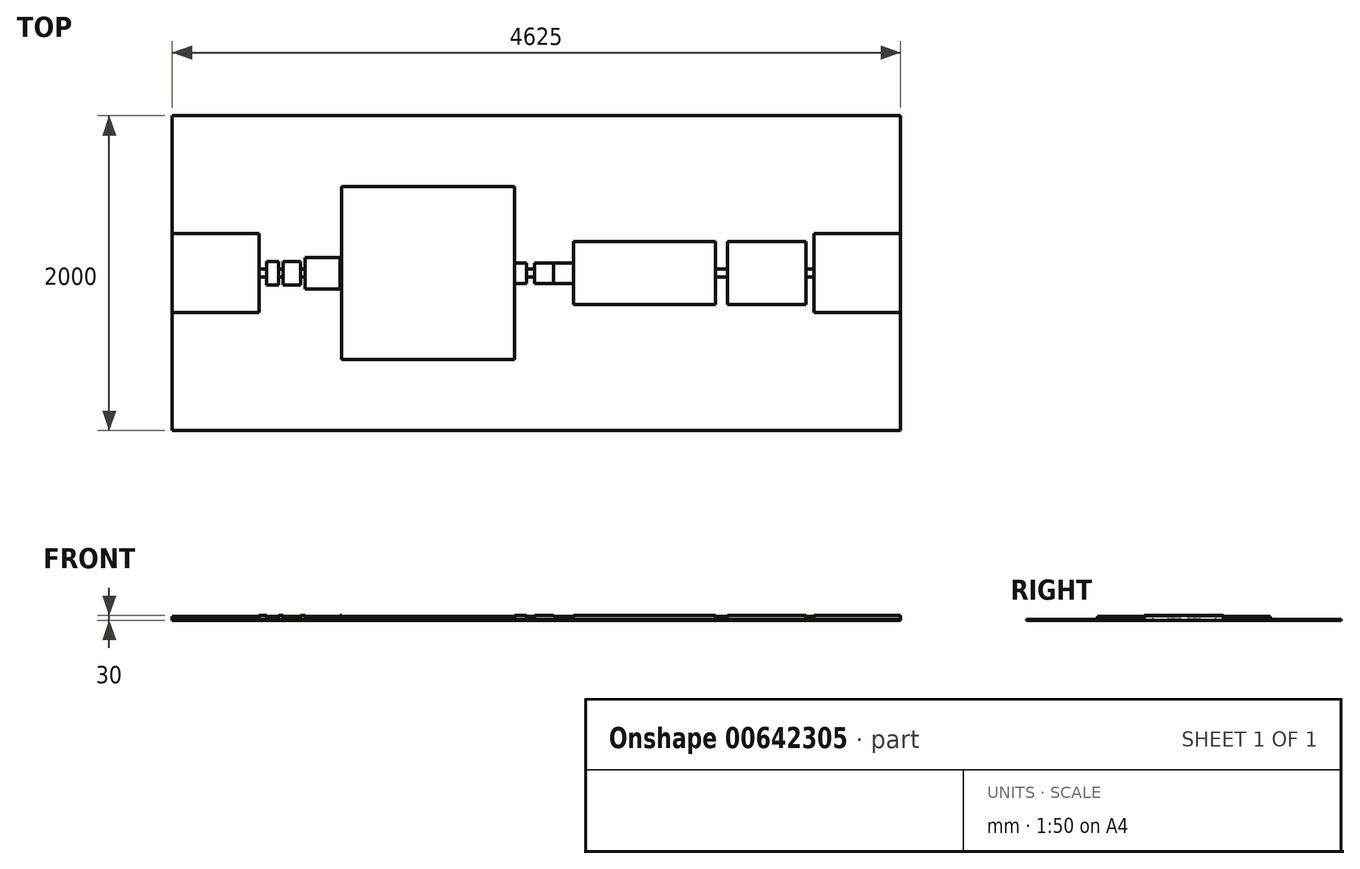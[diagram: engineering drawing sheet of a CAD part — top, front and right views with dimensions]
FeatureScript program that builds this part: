
annotation { "Feature Type Name" : "Feature", "Feature Type Description" : "" }
export const myFeature = defineFeature(function(context is Context, id is Id, definition is map)
    precondition{}
    {
        {
            var Q0;
            Q0=qCreatedBy(makeId("Top.planeOp"),FACE);
            var sketch = newSketch(context, id + "F0", { "sketchPlane" : qUnion([Q0])});
            skLineSegment(sketch, "E0.bottom", {"start": v(0, 1000) * mm, "end": v(4625, 1000) * mm});
            skLineSegment(sketch, "E0.top", {"start": v(0, -1000) * mm, "end": v(4625, -1000) * mm});
            skLineSegment(sketch, "E0.left", {"start": v(0, 1000) * mm, "end": v(0, -1000) * mm});
            skLineSegment(sketch, "E0.right", {"start": v(4625, 1000) * mm, "end": v(4625, -1000) * mm});
            skLineSegment(sketch, "E1", {"start": v(0, 0) * mm, "end": v(4625, 0) * mm, "construction": true});
            skLineSegment(sketch, "E2.bottom", {"start": v(550, -250) * mm, "end": v(0, -250) * mm});
            skLineSegment(sketch, "E2.top", {"start": v(550, 250) * mm, "end": v(0, 250) * mm});
            skLineSegment(sketch, "E2.left", {"start": v(550, -250) * mm, "end": v(550, 250) * mm});
            skLineSegment(sketch, "E2.right", {"start": v(0, -250) * mm, "end": v(0, 250) * mm});
            skPoint(sketch, "E2.middle", {"position": v(275, 0) * mm});
            skLineSegment(sketch, "E3.bottom", {"start": v(2175, -550) * mm, "end": v(1075, -550) * mm});
            skLineSegment(sketch, "E3.top", {"start": v(2175, 550) * mm, "end": v(1075, 550) * mm});
            skLineSegment(sketch, "E3.left", {"start": v(2175, -550) * mm, "end": v(2175, 550) * mm});
            skLineSegment(sketch, "E3.right", {"start": v(1075, -550) * mm, "end": v(1075, 550) * mm});
            skPoint(sketch, "E3.middle", {"position": v(1625, 0) * mm});
            skLineSegment(sketch, "E4.bottom", {"start": v(4625, -250) * mm, "end": v(4075, -250) * mm});
            skLineSegment(sketch, "E4.top", {"start": v(4625, 250) * mm, "end": v(4075, 250) * mm});
            skLineSegment(sketch, "E4.left", {"start": v(4625, -250) * mm, "end": v(4625, 250) * mm});
            skLineSegment(sketch, "E4.right", {"start": v(4075, -250) * mm, "end": v(4075, 250) * mm});
            skPoint(sketch, "E4.middle", {"position": v(4350, 0) * mm});
            skLineSegment(sketch, "E5.bottom", {"start": v(675, -75) * mm, "end": v(600, -75) * mm});
            skLineSegment(sketch, "E5.top", {"start": v(675, 75) * mm, "end": v(600, 75) * mm});
            skLineSegment(sketch, "E5.left", {"start": v(675, -75) * mm, "end": v(675, 75) * mm});
            skLineSegment(sketch, "E5.right", {"start": v(600, -75) * mm, "end": v(600, 75) * mm});
            skPoint(sketch, "E5.middle", {"position": v(637.5, 0) * mm});
            skLineSegment(sketch, "E6.bottom", {"start": v(600, -25) * mm, "end": v(550, -25) * mm});
            skLineSegment(sketch, "E6.top", {"start": v(600, 25) * mm, "end": v(550, 25) * mm});
            skLineSegment(sketch, "E6.left", {"start": v(600, -25) * mm, "end": v(600, 25) * mm});
            skLineSegment(sketch, "E6.right", {"start": v(550, -25) * mm, "end": v(550, 25) * mm});
            skPoint(sketch, "E6.middle", {"position": v(575, 0) * mm});
            skLineSegment(sketch, "E7.bottom", {"start": v(675, 25) * mm, "end": v(705, 25) * mm});
            skLineSegment(sketch, "E7.top", {"start": v(675, -25) * mm, "end": v(705, -25) * mm});
            skLineSegment(sketch, "E7.left", {"start": v(675, 25) * mm, "end": v(675, -25) * mm});
            skLineSegment(sketch, "E7.right", {"start": v(705, 25) * mm, "end": v(705, -25) * mm});
            skPoint(sketch, "E7.middle", {"position": v(690, 0) * mm});
            skLineSegment(sketch, "E8.bottom", {"start": v(705, 75) * mm, "end": v(815, 75) * mm});
            skLineSegment(sketch, "E8.top", {"start": v(705, -75) * mm, "end": v(815, -75) * mm});
            skLineSegment(sketch, "E8.left", {"start": v(705, 75) * mm, "end": v(705, -75) * mm});
            skLineSegment(sketch, "E8.right", {"start": v(815, 75) * mm, "end": v(815, -75) * mm});
            skPoint(sketch, "E8.middle", {"position": v(760, 0) * mm});
            skLineSegment(sketch, "E9.bottom", {"start": v(815, 25) * mm, "end": v(845, 25) * mm});
            skLineSegment(sketch, "E9.top", {"start": v(815, -25) * mm, "end": v(845, -25) * mm});
            skLineSegment(sketch, "E9.left", {"start": v(815, 25) * mm, "end": v(815, -25) * mm});
            skLineSegment(sketch, "E9.right", {"start": v(845, 25) * mm, "end": v(845, -25) * mm});
            skPoint(sketch, "E9.middle", {"position": v(830, 0) * mm});
            skLineSegment(sketch, "E10.bottom", {"start": v(845, 100) * mm, "end": v(1065, 100) * mm});
            skLineSegment(sketch, "E10.top", {"start": v(845, -100) * mm, "end": v(1065, -100) * mm});
            skLineSegment(sketch, "E10.left", {"start": v(845, 100) * mm, "end": v(845, -100) * mm});
            skLineSegment(sketch, "E10.right", {"start": v(1065, 100) * mm, "end": v(1065, -100) * mm});
            skPoint(sketch, "E10.middle", {"position": v(955, 0) * mm});
            skLineSegment(sketch, "E11.bottom", {"start": v(1065, 25) * mm, "end": v(1075, 25) * mm});
            skLineSegment(sketch, "E11.top", {"start": v(1065, -25) * mm, "end": v(1075, -25) * mm});
            skLineSegment(sketch, "E11.left", {"start": v(1065, 25) * mm, "end": v(1065, -25) * mm});
            skLineSegment(sketch, "E11.right", {"start": v(1075, 25) * mm, "end": v(1075, -25) * mm});
            skPoint(sketch, "E11.middle", {"position": v(1070, 0) * mm});
            skLineSegment(sketch, "E12.bottom", {"start": v(3450, -200) * mm, "end": v(2550, -200) * mm});
            skLineSegment(sketch, "E12.top", {"start": v(3450, 200) * mm, "end": v(2550, 200) * mm});
            skLineSegment(sketch, "E12.left", {"start": v(3450, -200) * mm, "end": v(3450, 200) * mm});
            skLineSegment(sketch, "E12.right", {"start": v(2550, -200) * mm, "end": v(2550, 200) * mm});
            skPoint(sketch, "E12.middle", {"position": v(3000, 0) * mm});
            skLineSegment(sketch, "E13.bottom", {"start": v(2075, -450) * mm, "end": v(1175, -450) * mm, "construction": true});
            skLineSegment(sketch, "E13.top", {"start": v(2075, 450) * mm, "end": v(1175, 450) * mm, "construction": true});
            skLineSegment(sketch, "E13.left", {"start": v(2075, -450) * mm, "end": v(2075, 450) * mm, "construction": true});
            skLineSegment(sketch, "E13.right", {"start": v(1175, -450) * mm, "end": v(1175, 450) * mm, "construction": true});
            skLineSegment(sketch, "E14.bottom", {"start": v(4025, -200) * mm, "end": v(3525, -200) * mm});
            skLineSegment(sketch, "E14.top", {"start": v(4025, 200) * mm, "end": v(3525, 200) * mm});
            skLineSegment(sketch, "E14.left", {"start": v(4025, -200) * mm, "end": v(4025, 200) * mm});
            skLineSegment(sketch, "E14.right", {"start": v(3525, -200) * mm, "end": v(3525, 200) * mm});
            skPoint(sketch, "E14.middle", {"position": v(3775, 0) * mm});
            skLineSegment(sketch, "E15.bottom", {"start": v(4025, 25) * mm, "end": v(4075, 25) * mm});
            skLineSegment(sketch, "E15.top", {"start": v(4025, -25) * mm, "end": v(4075, -25) * mm});
            skLineSegment(sketch, "E15.left", {"start": v(4025, 25) * mm, "end": v(4025, -25) * mm});
            skLineSegment(sketch, "E15.right", {"start": v(4075, 25) * mm, "end": v(4075, -25) * mm});
            skPoint(sketch, "E15.middle", {"position": v(4050, 0) * mm});
            skLineSegment(sketch, "E16.bottom", {"start": v(3450, 25) * mm, "end": v(3525, 25) * mm});
            skLineSegment(sketch, "E16.top", {"start": v(3450, -25) * mm, "end": v(3525, -25) * mm});
            skLineSegment(sketch, "E16.left", {"start": v(3450, 25) * mm, "end": v(3450, -25) * mm});
            skLineSegment(sketch, "E16.right", {"start": v(3525, 25) * mm, "end": v(3525, -25) * mm});
            skLineSegment(sketch, "E17.bottom", {"start": v(2550, -65) * mm, "end": v(2420, -65) * mm});
            skLineSegment(sketch, "E17.top", {"start": v(2550, 65) * mm, "end": v(2420, 65) * mm});
            skLineSegment(sketch, "E17.left", {"start": v(2550, -65) * mm, "end": v(2550, 65) * mm});
            skLineSegment(sketch, "E17.right", {"start": v(2420, -65) * mm, "end": v(2420, 65) * mm});
            skPoint(sketch, "E17.middle", {"position": v(2485, 0) * mm});
            skLineSegment(sketch, "E18.bottom", {"start": v(2250, -65) * mm, "end": v(2175, -65) * mm});
            skLineSegment(sketch, "E18.top", {"start": v(2250, 65) * mm, "end": v(2175, 65) * mm});
            skLineSegment(sketch, "E18.left", {"start": v(2250, -65) * mm, "end": v(2250, 65) * mm});
            skLineSegment(sketch, "E18.right", {"start": v(2175, -65) * mm, "end": v(2175, 65) * mm});
            skPoint(sketch, "E18.middle", {"position": v(2212.5, 0) * mm});
            skLineSegment(sketch, "E19.bottom", {"start": v(2420, -65) * mm, "end": v(2300, -65) * mm});
            skLineSegment(sketch, "E19.top", {"start": v(2420, 65) * mm, "end": v(2300, 65) * mm});
            skLineSegment(sketch, "E19.right", {"start": v(2300, -65) * mm, "end": v(2300, 65) * mm});
            skPoint(sketch, "E19.middle", {"position": v(2360, 0) * mm});
            skLineSegment(sketch, "E20.bottom", {"start": v(2250, 25) * mm, "end": v(2300, 25) * mm});
            skLineSegment(sketch, "E20.top", {"start": v(2250, -25) * mm, "end": v(2300, -25) * mm});
            skLineSegment(sketch, "E20.left", {"start": v(2250, 25) * mm, "end": v(2250, -25) * mm});
            skLineSegment(sketch, "E20.right", {"start": v(2300, 25) * mm, "end": v(2300, -25) * mm});
            skPoint(sketch, "E20.middle", {"position": v(2275, 0) * mm});
            skSolve(sketch);
        }
        {
            var Q0;
            {var subQ3=sQuery(id+"F0.wireOp",EDGE,"E2.bottom");Q0=makeQuery(id+"F0.imprint","IMPRINT",FACE,{"disambiguationData":[TD([[makeQuery(id+"F0.imprint","IMPRINT",EDGE,{"derivedFrom":subQ3}),-1.0]])]});}
            var Q1;
            Q1=makeQuery(id+"F0.imprint","IMPRINT",FACE,{"disambiguationData":[TD([[makeQuery(id+"F0.imprint","IMPRINT",EDGE,{"derivedFrom":sQuery(id+"F0.wireOp",EDGE,"E6.bottom")}),-1.0]])]});
            var Q2;
            {var subQ3=sQuery(id+"F0.wireOp",EDGE,"E5.bottom");Q2=makeQuery(id+"F0.imprint","IMPRINT",FACE,{"disambiguationData":[TD([[makeQuery(id+"F0.imprint","IMPRINT",EDGE,{"derivedFrom":subQ3}),-1.0]])]});}
            var Q3;
            {var subQ0=sQuery(id+"F0.wireOp",EDGE,"E7.bottom");Q3=makeQuery(id+"F0.imprint","IMPRINT",FACE,{"disambiguationData":[TD([[makeQuery(id+"F0.imprint","IMPRINT",EDGE,{"derivedFrom":subQ0}),-1.0]])]});}
            var Q4;
            {var subQ3=sQuery(id+"F0.wireOp",EDGE,"E8.bottom");Q4=makeQuery(id+"F0.imprint","IMPRINT",FACE,{"disambiguationData":[TD([[makeQuery(id+"F0.imprint","IMPRINT",EDGE,{"derivedFrom":subQ3}),-1.0]])]});}
            var Q5;
            {var subQ0=sQuery(id+"F0.wireOp",EDGE,"E9.bottom");Q5=makeQuery(id+"F0.imprint","IMPRINT",FACE,{"disambiguationData":[TD([[makeQuery(id+"F0.imprint","IMPRINT",EDGE,{"derivedFrom":subQ0}),-1.0]])]});}
            var Q6;
            {var subQ3=sQuery(id+"F0.wireOp",EDGE,"E10.bottom");Q6=makeQuery(id+"F0.imprint","IMPRINT",FACE,{"disambiguationData":[TD([[makeQuery(id+"F0.imprint","IMPRINT",EDGE,{"derivedFrom":subQ3}),-1.0]])]});}
            var Q7;
            Q7=makeQuery(id+"F0.imprint","IMPRINT",FACE,{"disambiguationData":[TD([[makeQuery(id+"F0.imprint","IMPRINT",EDGE,{"derivedFrom":sQuery(id+"F0.wireOp",EDGE,"E11.bottom")}),-1.0]])]});
            var Q8;
            {var subQ3=sQuery(id+"F0.wireOp",EDGE,"E3.bottom");Q8=makeQuery(id+"F0.imprint","IMPRINT",FACE,{"disambiguationData":[TD([[makeQuery(id+"F0.imprint","IMPRINT",EDGE,{"derivedFrom":subQ3}),-1.0]])]});}
            var Q9;
            {var subQ3=sQuery(id+"F0.wireOp",EDGE,"E18.bottom");Q9=makeQuery(id+"F0.imprint","IMPRINT",FACE,{"disambiguationData":[TD([[makeQuery(id+"F0.imprint","IMPRINT",EDGE,{"derivedFrom":subQ3}),-1.0]])]});}
            var Q10;
            Q10=makeQuery(id+"F0.imprint","IMPRINT",FACE,{"disambiguationData":[TD([[makeQuery(id+"F0.imprint","IMPRINT",EDGE,{"derivedFrom":sQuery(id+"F0.wireOp",EDGE,"E20.bottom")}),-1.0]])]});
            var Q11;
            {var subQ1=sQuery(id+"F0.wireOp",EDGE,"E19.bottom");Q11=makeQuery(id+"F0.imprint","IMPRINT",FACE,{"disambiguationData":[TD([[makeQuery(id+"F0.imprint","IMPRINT",EDGE,{"derivedFrom":subQ1}),-1.0]])]});}
            var Q12;
            Q12=makeQuery(id+"F0.imprint","IMPRINT",FACE,{"disambiguationData":[TD([[makeQuery(id+"F0.imprint","IMPRINT",EDGE,{"derivedFrom":sQuery(id+"F0.wireOp",EDGE,"E17.bottom")}),-1.0]])]});
            var Q13;
            {var subQ3=sQuery(id+"F0.wireOp",EDGE,"E12.bottom");Q13=makeQuery(id+"F0.imprint","IMPRINT",FACE,{"disambiguationData":[TD([[makeQuery(id+"F0.imprint","IMPRINT",EDGE,{"derivedFrom":subQ3}),-1.0]])]});}
            var Q14;
            Q14=makeQuery(id+"F0.imprint","IMPRINT",FACE,{"disambiguationData":[TD([[makeQuery(id+"F0.imprint","IMPRINT",EDGE,{"derivedFrom":sQuery(id+"F0.wireOp",EDGE,"E16.bottom")}),-1.0]])]});
            var Q15;
            {var subQ3=sQuery(id+"F0.wireOp",EDGE,"E14.bottom");Q15=makeQuery(id+"F0.imprint","IMPRINT",FACE,{"disambiguationData":[TD([[makeQuery(id+"F0.imprint","IMPRINT",EDGE,{"derivedFrom":subQ3}),-1.0]])]});}
            var Q16;
            Q16=makeQuery(id+"F0.imprint","IMPRINT",FACE,{"disambiguationData":[TD([[makeQuery(id+"F0.imprint","IMPRINT",EDGE,{"derivedFrom":sQuery(id+"F0.wireOp",EDGE,"E15.bottom")}),-1.0]])]});
            var Q17;
            {var subQ1=sQuery(id+"F0.wireOp",EDGE,"E4.bottom");Q17=makeQuery(id+"F0.imprint","IMPRINT",FACE,{"disambiguationData":[TD([[makeQuery(id+"F0.imprint","IMPRINT",EDGE,{"derivedFrom":subQ1}),-1.0]])]});}
            extrude(context, id + "F1", {"entities" : qUnion([Q0, Q1, Q2, Q3, Q4, Q5, Q6, Q7, Q8, Q9, Q10, Q11, Q12, Q13, Q14, Q15, Q16, Q17]), "depth" : 25 * mm, "offsetDistance" : 25 * mm});
        }
        {
            var Q0;
            Q0 = qSketchRegion(id + "F0", true);
            extrude(context, id + "F2", {"entities" : qUnion([Q0]), "operationType" : NewBodyOperationType.ADD, "depth" : 5 * mm, "offsetDistance" : 25 * mm});
        }
        {
            var Q0;
            Q0=makeQuery(id+"F0.imprint","IMPRINT",FACE,{"disambiguationData":[TD([[makeQuery(id+"F0.imprint","IMPRINT",EDGE,{"derivedFrom":sQuery(id+"F0.wireOp",EDGE,"E6.bottom")}),-1.0]])]});
            var Q1;
            {var subQ0=sQuery(id+"F0.wireOp",EDGE,"E7.bottom");Q1=makeQuery(id+"F0.imprint","IMPRINT",FACE,{"disambiguationData":[TD([[makeQuery(id+"F0.imprint","IMPRINT",EDGE,{"derivedFrom":subQ0}),-1.0]])]});}
            var Q2;
            {var subQ0=sQuery(id+"F0.wireOp",EDGE,"E9.bottom");Q2=makeQuery(id+"F0.imprint","IMPRINT",FACE,{"disambiguationData":[TD([[makeQuery(id+"F0.imprint","IMPRINT",EDGE,{"derivedFrom":subQ0}),-1.0]])]});}
            var Q3;
            Q3=makeQuery(id+"F0.imprint","IMPRINT",FACE,{"disambiguationData":[TD([[makeQuery(id+"F0.imprint","IMPRINT",EDGE,{"derivedFrom":sQuery(id+"F0.wireOp",EDGE,"E11.bottom")}),-1.0]])]});
            var Q4;
            {var subQ3=sQuery(id+"F0.wireOp",EDGE,"E18.bottom");Q4=makeQuery(id+"F0.imprint","IMPRINT",FACE,{"disambiguationData":[TD([[makeQuery(id+"F0.imprint","IMPRINT",EDGE,{"derivedFrom":subQ3}),-1.0]])]});}
            var Q5;
            {var subQ1=sQuery(id+"F0.wireOp",EDGE,"E19.bottom");Q5=makeQuery(id+"F0.imprint","IMPRINT",FACE,{"disambiguationData":[TD([[makeQuery(id+"F0.imprint","IMPRINT",EDGE,{"derivedFrom":subQ1}),-1.0]])]});}
            var Q6;
            {var subQ3=sQuery(id+"F0.wireOp",EDGE,"E12.bottom");Q6=makeQuery(id+"F0.imprint","IMPRINT",FACE,{"disambiguationData":[TD([[makeQuery(id+"F0.imprint","IMPRINT",EDGE,{"derivedFrom":subQ3}),-1.0]])]});}
            var Q7;
            {var subQ3=sQuery(id+"F0.wireOp",EDGE,"E14.bottom");Q7=makeQuery(id+"F0.imprint","IMPRINT",FACE,{"disambiguationData":[TD([[makeQuery(id+"F0.imprint","IMPRINT",EDGE,{"derivedFrom":subQ3}),-1.0]])]});}
            var Q8;
            {var subQ1=sQuery(id+"F0.wireOp",EDGE,"E4.bottom");Q8=makeQuery(id+"F0.imprint","IMPRINT",FACE,{"disambiguationData":[TD([[makeQuery(id+"F0.imprint","IMPRINT",EDGE,{"derivedFrom":subQ1}),-1.0]])]});}
            extrude(context, id + "F3", {"entities" : qUnion([Q0, Q1, Q2, Q3, Q4, Q5, Q6, Q7, Q8]), "operationType" : NewBodyOperationType.ADD, "depth" : 30 * mm, "offsetDistance" : 25 * mm});
        }
    });
